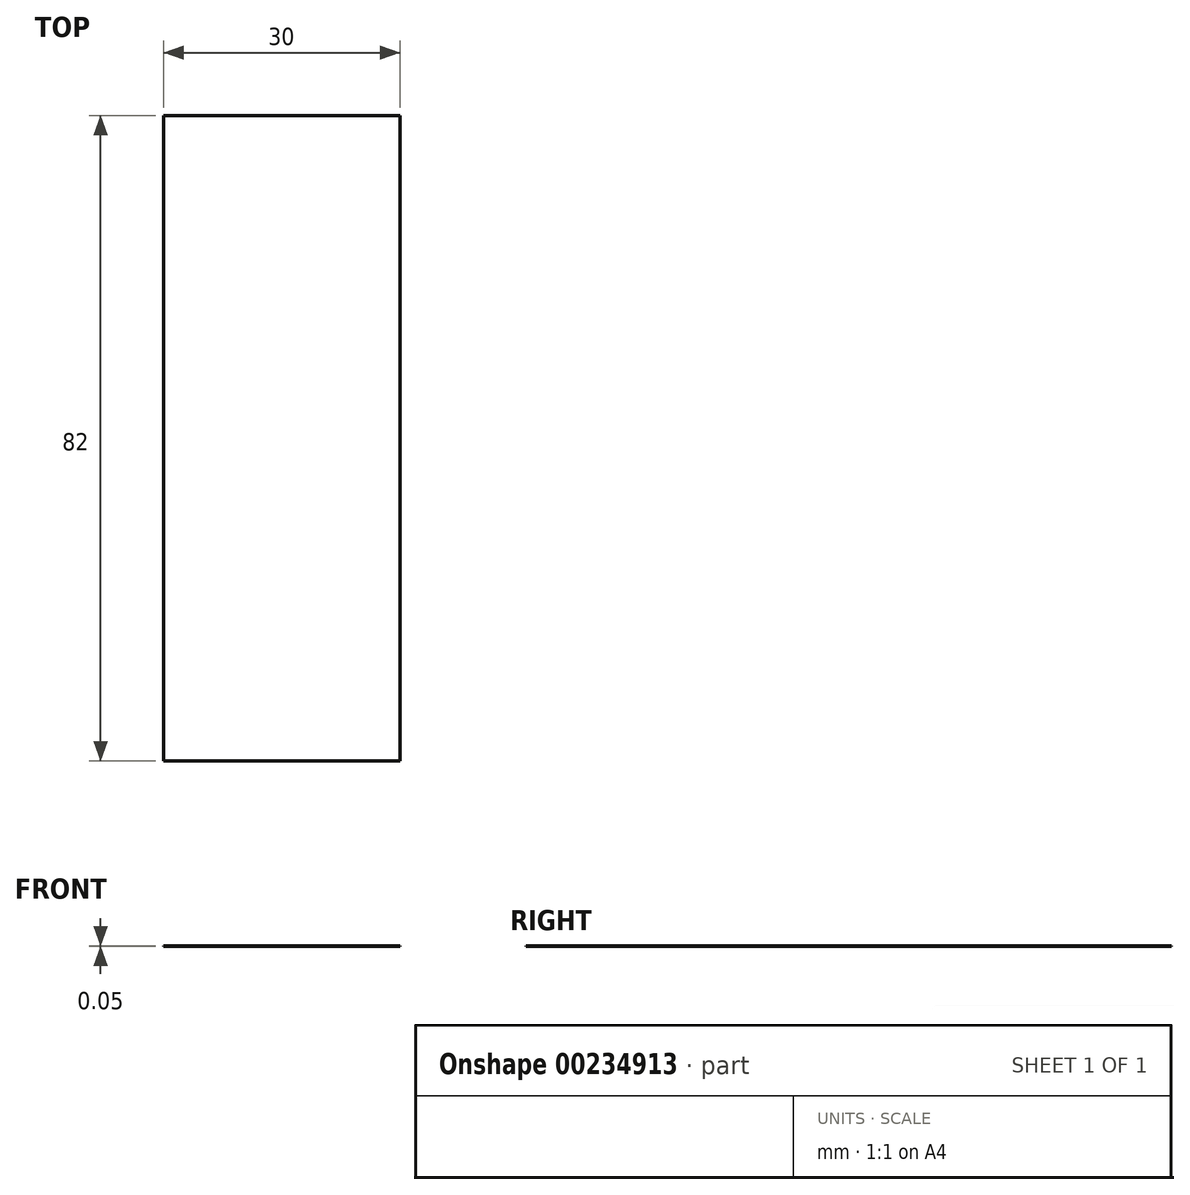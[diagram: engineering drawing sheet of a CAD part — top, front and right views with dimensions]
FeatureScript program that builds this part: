
annotation { "Feature Type Name" : "Feature", "Feature Type Description" : "" }
export const myFeature = defineFeature(function(context is Context, id is Id, definition is map)
    precondition{}
    {
        {
            var Q0;
            Q0=qCreatedBy(makeId("Top.planeOp"),FACE);
            var sketch = newSketch(context, id + "F0", { "sketchPlane" : qUnion([Q0])});
            skLineSegment(sketch, "E0.bottom", {"start": v(15, -41) * mm, "end": v(-15, -41) * mm});
            skLineSegment(sketch, "E0.top", {"start": v(15, 41) * mm, "end": v(-15, 41) * mm});
            skLineSegment(sketch, "E0.left", {"start": v(15, -41) * mm, "end": v(15, 41) * mm});
            skLineSegment(sketch, "E0.right", {"start": v(-15, -41) * mm, "end": v(-15, 41) * mm});
            skPoint(sketch, "E0.middle", {"position": v(0, 0) * mm});
            skSolve(sketch);
        }
        {
            var Q0;
            Q0 = qSketchRegion(id + "F0", true);
            extrude(context, id + "F1", {"entities" : qUnion([Q0]), "depth" : 0.05 * mm});
        }
    });
